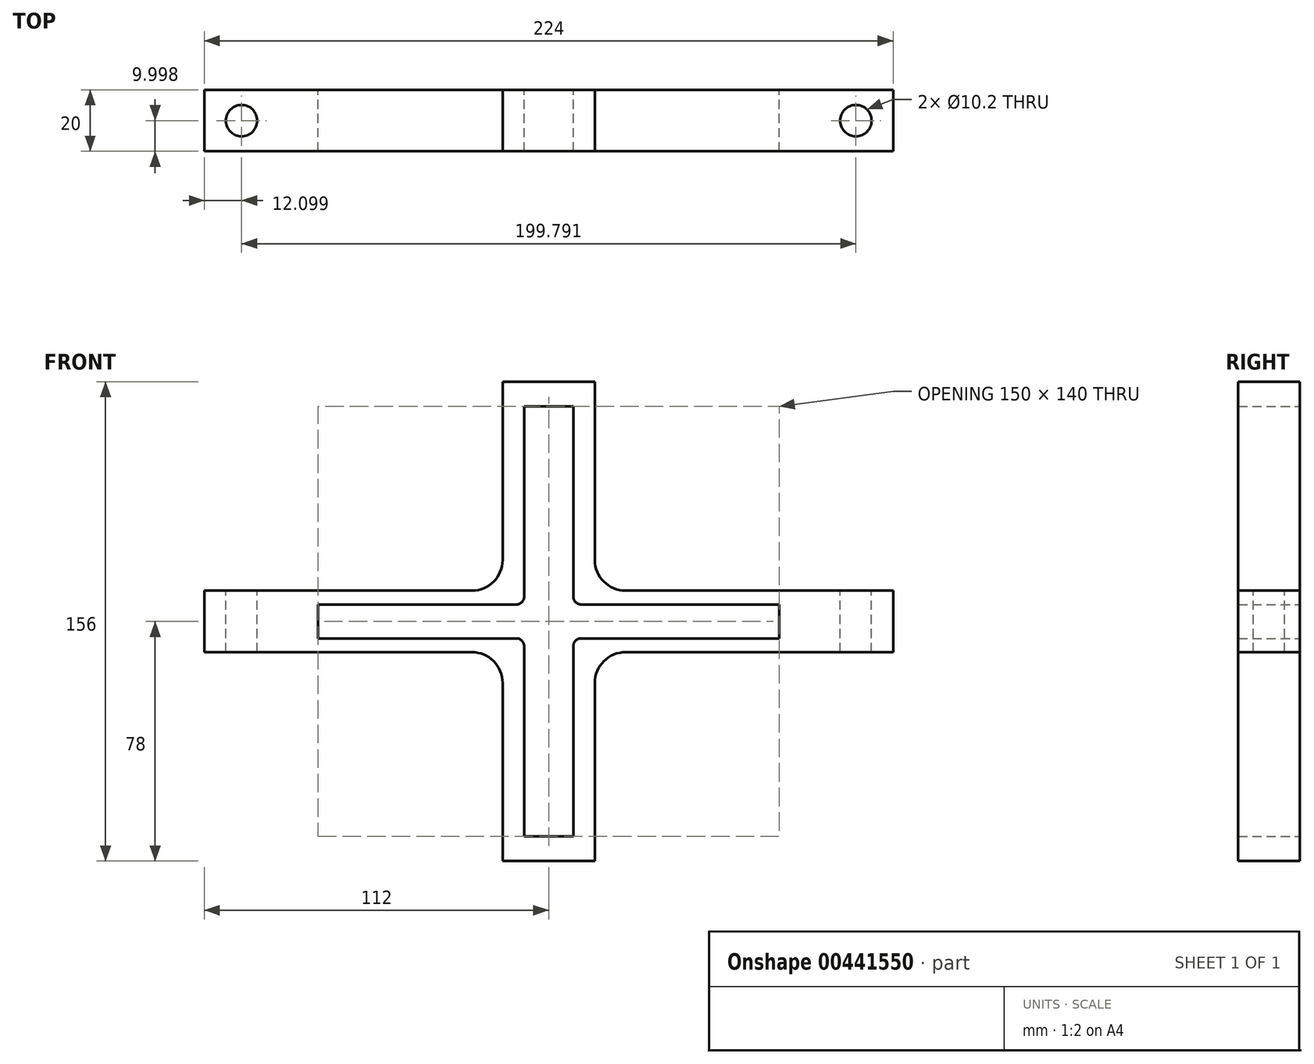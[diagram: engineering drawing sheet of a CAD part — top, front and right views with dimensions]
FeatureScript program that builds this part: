
annotation { "Feature Type Name" : "Feature", "Feature Type Description" : "" }
export const myFeature = defineFeature(function(context is Context, id is Id, definition is map)
    precondition{}
    {
        {
            var Q0;
            Q0=qCreatedBy(makeId("Front.planeOp"),FACE);
            var sketch = newSketch(context, id + "F0", { "sketchPlane" : qUnion([Q0])});
            skLineSegment(sketch, "E0.bottom", {"start": v(112, -10) * mm, "end": v(15, -10) * mm});
            skLineSegment(sketch, "E0.top", {"start": v(112, 10) * mm, "end": v(15, 10) * mm});
            skLineSegment(sketch, "E0.left", {"start": v(112, -10) * mm, "end": v(112, 10) * mm});
            skLineSegment(sketch, "E0.right", {"start": v(-112, -10) * mm, "end": v(-112, 10) * mm});
            skPoint(sketch, "E0.middle", {"position": v(0, 0) * mm});
            skLineSegment(sketch, "E1.bottom", {"start": v(15, 78) * mm, "end": v(-15, 78) * mm});
            skLineSegment(sketch, "E1.top", {"start": v(15, -78) * mm, "end": v(-15, -78) * mm});
            skLineSegment(sketch, "E1.left", {"start": v(15, 78) * mm, "end": v(15, 10) * mm});
            skLineSegment(sketch, "E1.right", {"start": v(-15, 78) * mm, "end": v(-15, 10) * mm});
            skLineSegment(sketch, "E2.trimOffspring", {"start": v(-15, 10) * mm, "end": v(-112, 10) * mm});
            skLineSegment(sketch, "E3.trimOffspring", {"start": v(-15, -10) * mm, "end": v(-15, -78) * mm});
            skLineSegment(sketch, "E4.trimOffspring", {"start": v(-15, -10) * mm, "end": v(-112, -10) * mm});
            skLineSegment(sketch, "E5.trimOffspring", {"start": v(15, -10) * mm, "end": v(15, -78) * mm});
            skLineSegment(sketch, "E6.bottom", {"start": v(75, -5.5) * mm, "end": v(8, -5.5) * mm});
            skLineSegment(sketch, "E6.top", {"start": v(75, 5.5) * mm, "end": v(8, 5.5) * mm});
            skLineSegment(sketch, "E6.left", {"start": v(75, -5.5) * mm, "end": v(75, 5.5) * mm});
            skLineSegment(sketch, "E6.right", {"start": v(-75, -5.5) * mm, "end": v(-75, 5.5) * mm});
            skLineSegment(sketch, "E7.bottom", {"start": v(-8, 70) * mm, "end": v(8, 70) * mm});
            skLineSegment(sketch, "E7.top", {"start": v(-8, -70) * mm, "end": v(8, -70) * mm});
            skLineSegment(sketch, "E7.left", {"start": v(-8, 70) * mm, "end": v(-8, 5.5) * mm});
            skLineSegment(sketch, "E7.right", {"start": v(8, 70) * mm, "end": v(8, 5.5) * mm});
            skLineSegment(sketch, "E8.trimOffspring", {"start": v(-8, -5.5) * mm, "end": v(-8, -70) * mm});
            skLineSegment(sketch, "E9.trimOffspring", {"start": v(-8, 5.5) * mm, "end": v(-75, 5.5) * mm});
            skLineSegment(sketch, "E10.trimOffspring", {"start": v(8, -5.5) * mm, "end": v(8, -70) * mm});
            skLineSegment(sketch, "E11.trimOffspring", {"start": v(-8, -5.5) * mm, "end": v(-75, -5.5) * mm});
            skSolve(sketch);
        }
        {
            var Q0;
            Q0 = qSketchRegion(id + "F0", true);
            extrude(context, id + "F1", {"entities" : qUnion([Q0]), "depth" : 20 * mm});
        }
        {
            var Q0;
            Q0=makeQuery(id+"F1.opExtrude","SWEPT_EDGE",EDGE,{"disambiguationData":[OSD([sQuery(id+"F0.wireOp",EDGE,"E0.top"),sQuery(id+"F0.wireOp",EDGE,"E1.left")])]});
            var Q1;
            Q1=makeQuery(id+"F1.opExtrude","SWEPT_EDGE",EDGE,{"disambiguationData":[OSD([sQuery(id+"F0.wireOp",EDGE,"E1.right"),sQuery(id+"F0.wireOp",EDGE,"E2.trimOffspring")])]});
            var Q2;
            Q2=makeQuery(id+"F1.opExtrude","SWEPT_EDGE",EDGE,{"disambiguationData":[OSD([sQuery(id+"F0.wireOp",EDGE,"E3.trimOffspring"),sQuery(id+"F0.wireOp",EDGE,"E4.trimOffspring")])]});
            var Q3;
            Q3=makeQuery(id+"F1.opExtrude","SWEPT_EDGE",EDGE,{"disambiguationData":[OSD([sQuery(id+"F0.wireOp",EDGE,"E0.bottom"),sQuery(id+"F0.wireOp",EDGE,"E5.trimOffspring")])]});
            fillet(context, id + "F2", {"entities" : qUnion([Q0, Q1, Q2, Q3]), "radius" : 10 * mm, "tangentPropagation" : true, "allowEdgeOverflow" : false});
        }
        {
            var Q0;
            Q0=makeQuery(id+"F1.opExtrude","SWEPT_EDGE",EDGE,{"disambiguationData":[OSD([sQuery(id+"F0.wireOp",EDGE,"E7.left"),sQuery(id+"F0.wireOp",EDGE,"E9.trimOffspring")])]});
            var Q1;
            Q1=makeQuery(id+"F1.opExtrude","SWEPT_EDGE",EDGE,{"disambiguationData":[OSD([sQuery(id+"F0.wireOp",EDGE,"E6.top"),sQuery(id+"F0.wireOp",EDGE,"E7.right")])]});
            var Q2;
            Q2=makeQuery(id+"F1.opExtrude","SWEPT_EDGE",EDGE,{"disambiguationData":[OSD([sQuery(id+"F0.wireOp",EDGE,"E6.bottom"),sQuery(id+"F0.wireOp",EDGE,"E10.trimOffspring")])]});
            var Q3;
            Q3=makeQuery(id+"F1.opExtrude","SWEPT_EDGE",EDGE,{"disambiguationData":[OSD([sQuery(id+"F0.wireOp",EDGE,"E8.trimOffspring"),sQuery(id+"F0.wireOp",EDGE,"E11.trimOffspring")])]});
            fillet(context, id + "F3", {"entities" : qUnion([Q0, Q1, Q2, Q3]), "radius" : 2.54 * mm, "tangentPropagation" : true, "allowEdgeOverflow" : false});
        }
        {
            var Q0;
            Q0=makeQuery(id+"F1.opExtrude","SWEPT_FACE",FACE,{"disambiguationData":[OSD([sQuery(id+"F0.wireOp",EDGE,"E2.trimOffspring")])]});
            var sketch = newSketch(context, id + "F4", { "sketchPlane" : qUnion([Q0])});
            skCircle(sketch, "E12", {"center": v(-99.9, -10) * mm, "radius": 5.1 * mm});
            skCircle(sketch, "E13", {"center": v(99.9, -10) * mm, "radius": 5.1 * mm});
            skSolve(sketch);
        }
        {
            var Q0;
            Q0 = qSketchRegion(id + "F4", true);
            extrude(context, id + "F5", {"entities" : qUnion([Q0]), "operationType" : NewBodyOperationType.REMOVE, "oppositeDirection" : true, "depth" : 105.92 * mm});
        }
    });
